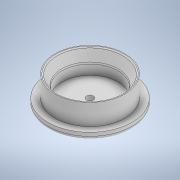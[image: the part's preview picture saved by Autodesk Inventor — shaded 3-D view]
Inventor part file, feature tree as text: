
AUTODESK INVENTOR PART (.ipt)
format: ipt  version: 2022 (Build 260153000, 153)  size: 156,672 bytes
history: native  units: in
note: dims shown in document units (in); Inventor stores cm internally (conversion verified against a paired STEP export)
features: extrude x3, fillet x3, sketch x3, chamfer x1
ambient origin geometry x8: Origin, YZ Plane, XZ Plane, XY Plane, X Axis, Y Axis, Z Axis, Center Point
bodies: Solid1 (feature_tree)
feature tree (10):
  extrude  "Extrusion1"  Depth=0.0394in TaperAngle=0.0deg
  fillet  "Fillet1"  Radius=0.0197in
  extrude  "Extrusion2"  Depth=0.0394in TaperAngle=0.0deg
  extrude  "Extrusion3"  Depth=0.0197in
  chamfer  "Chamfer1"  Distance=0.1181in
  fillet  "Fillet2"  Radius=0.0295in
  fillet  "Fillet3"  Radius=0.0079in
  sketch  "Sketch1"  dims[d0=0.4724in d1=0.0394in d2=0.0in d3=0.0197in]
  sketch  "Sketch2"  dims[d4=0.0394in d5=0.0394in d6=0.0in]
  sketch  "Sketch3"  dims[d7=0.3937in d8=0.315in d9=0.1181in d10=0.0in d11=0.0295in d12=0.0591in d13=45.0deg d14=0.0079in d15=0.0197in]
